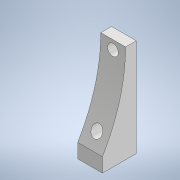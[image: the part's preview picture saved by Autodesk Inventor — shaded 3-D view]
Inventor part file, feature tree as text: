
AUTODESK INVENTOR PART (.ipt)
format: ipt  version: 2022 (Build 260153070, 153G)  size: 162,304 bytes
history: native  units: in
note: dims shown in document units (in); Inventor stores cm internally (conversion verified against a paired STEP export)
features: extrude x6, sketch x4, reference x2, other x2
ambient origin geometry x8: Origin, YZ Plane, XZ Plane, XY Plane, X Axis, Y Axis, Z Axis, Center Point
bodies: Solid1 (feature_tree)
feature tree (14):
  extrude  "Extrusion1"  Depth=0.1368in
  extrude  "Extrusion2"  Depth=0.1368in
  sketch  "Sketch3"  dims[d4=0.374in d5=0.0in d6=0.1181in]
  extrude  "Extrusion3"  Depth=0.1181in
  extrude  "Extrusion4"  Depth=0.3937in TaperAngle=0.0deg
  sketch  "Sketch4"  dims[d7=0.1575in d8=0.3937in d9=0.0in d10=0.3115in d11=0.0in d12=0.0492in d13=0.0in d14=0.1518in d15=0.0915in d16=0.1083in d17=0.2559in d18=0.1885in d19=0.0in d20=0.249in d21=0.0in]
  extrude  "Extrusion5"  Depth=0.3937in TaperAngle=0.0deg
  extrude  "Extrusion6"  Depth=0.3937in TaperAngle=0.0deg
  sketch  "Sketch1"  dims[d0=1.0807in d1=0.1368in]
  reference  "Reference1"
  reference  "Reference2"
  sketch  "Sketch2"  dims[d2=0.0945in d3=0.1368in]
  other  "Assembly1"
  other  "TT motor output:1"
